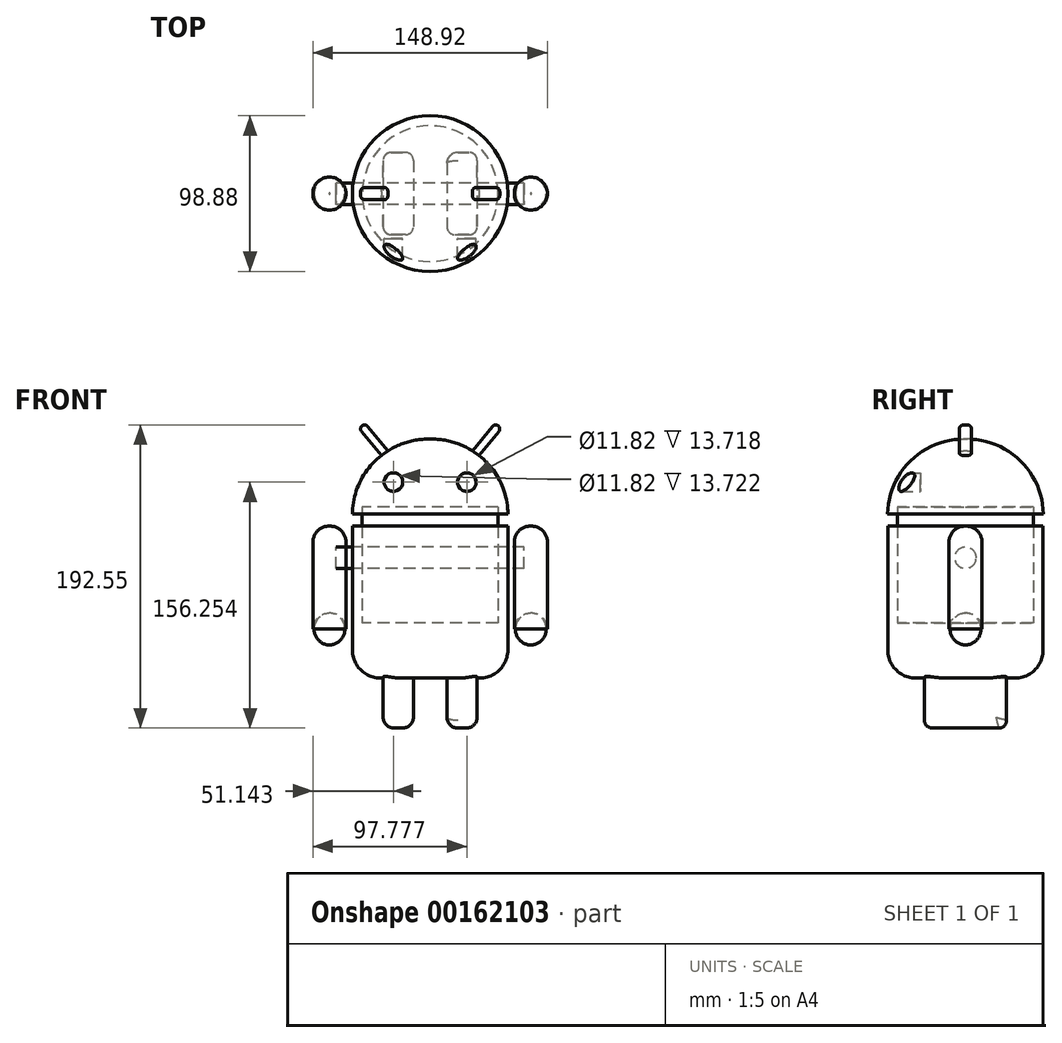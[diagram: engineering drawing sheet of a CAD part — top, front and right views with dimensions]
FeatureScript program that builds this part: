
annotation { "Feature Type Name" : "Feature", "Feature Type Description" : "" }
export const myFeature = defineFeature(function(context is Context, id is Id, definition is map)
    precondition{}
    {
        {
            var Q0;
            Q0=qCreatedBy(makeId("Top.planeOp"),FACE);
            var sketch = newSketch(context, id + "F0", { "sketchPlane" : qUnion([Q0])});
            skCircle(sketch, "E0", {"center": v(0, 0) * mm, "radius": 49.33 * mm});
            skSolve(sketch);
        }
        {
            var Q0;
            Q0=qSketchRegion(id+"F0",true);
            extrude(context, id + "F1", {"entities" : qUnion([Q0]), "depth" : 61.6 * mm, "hasSecondDirection" : true, "secondDirectionOppositeDirection" : true, "secondDirectionDepth" : 34.92 * mm});
        }
        {
            var Q0;
            Q0=makeQuery(id+"F1.opExtrude","CAP_FACE",FACE,{"disambiguationData":[OSD([sQuery(id+"F0.wireOp",EDGE,"E0")])],"isStart":false});
            var sketch = newSketch(context, id + "F2", { "sketchPlane" : qUnion([Q0])});
            skCircle(sketch, "E1", {"center": v(0, 0) * mm, "radius": 49.44 * mm});
            skSolve(sketch);
        }
        {
            var Q0;
            Q0=qSketchRegion(id+"F2",true);
            extrude(context, id + "F3", {"entities" : qUnion([Q0]), "depth" : 55.24 * mm, "hasSecondDirection" : true, "secondDirectionOppositeDirection" : false, "secondDirectionDepth" : 7.62 * mm});
        }
        {
            var Q0;
            Q0=makeQuery(id+"F3.opExtrude","CAP_EDGE",EDGE,{"disambiguationData":[OSD([sQuery(id+"F2.wireOp",EDGE,"E1")])],"isStart":false});
            fillet(context, id + "F4", {"entities" : qUnion([Q0]), "radius" : 48.26 * mm, "tangentPropagation" : true, "allowEdgeOverflow" : false});
        }
        {
            var Q0;
            Q0=makeQuery(id+"F1.opExtrude","CAP_EDGE",EDGE,{"disambiguationData":[OSD([sQuery(id+"F0.wireOp",EDGE,"E0")])],"isStart":true});
            fillet(context, id + "F5", {"entities" : qUnion([Q0]), "radius" : 17.78 * mm, "tangentPropagation" : true, "allowEdgeOverflow" : false});
        }
        {
            var Q0;
            Q0=qCreatedBy(makeId("Top.planeOp"),FACE);
            var sketch = newSketch(context, id + "F6", { "sketchPlane" : qUnion([Q0])});
            skCircle(sketch, "E2", {"center": v(-63.94, 0) * mm, "radius": 10.52 * mm});
            skCircle(sketch, "E3.MirrorC", {"center": v(63.94, 0) * mm, "radius": 10.52 * mm});
            skSolve(sketch);
        }
        {
            var Q0;
            Q0=qSketchRegion(id+"F6",true);
            extrude(context, id + "F7", {"entities" : qUnion([Q0]), "depth" : 61.6 * mm, "hasSecondDirection" : true, "secondDirectionOppositeDirection" : true, "secondDirectionDepth" : 13.97 * mm});
        }
        {
            var Q0;
            Q0=makeQuery(id+"F7.opExtrude","CAP_EDGE",EDGE,{"disambiguationData":[OSD([sQuery(id+"F6.wireOp",EDGE,"E2")])],"isStart":false});
            var Q1;
            Q1=makeQuery(id+"F7.opExtrude","CAP_EDGE",EDGE,{"disambiguationData":[OSD([sQuery(id+"F6.wireOp",EDGE,"E2")])],"isStart":true});
            var Q2;
            Q2=makeQuery(id+"F7.opExtrude","CAP_EDGE",EDGE,{"disambiguationData":[OSD([sQuery(id+"F6.wireOp",EDGE,"E3.MirrorC")])],"isStart":false});
            var Q3;
            Q3=makeQuery(id+"F7.opExtrude","CAP_EDGE",EDGE,{"disambiguationData":[OSD([sQuery(id+"F6.wireOp",EDGE,"E3.MirrorC")])],"isStart":true});
            fillet(context, id + "F8", {"entities" : qUnion([Q0, Q1, Q2, Q3]), "radius" : 10.16 * mm, "tangentPropagation" : true, "allowEdgeOverflow" : false});
        }
        {
            var Q0;
            Q0=qCreatedBy(makeId("Right.planeOp"),FACE);
            var sketch = newSketch(context, id + "F9", { "sketchPlane" : qUnion([Q0])});
            skCircle(sketch, "E4", {"center": v(0, 41.46) * mm, "radius": 6.83 * mm});
            skSolve(sketch);
        }
        {
            var Q0;
            Q0=qSketchRegion(id+"F9",true);
            extrude(context, id + "F10", {"entities" : qUnion([Q0]), "endBound" : BoundingType.SYMMETRIC, "depth" : 119.38 * mm});
        }
        {
            var Q0;
            Q0=qCreatedBy(makeId("Top.planeOp"),FACE);
            var sketch = newSketch(context, id + "F11", { "sketchPlane" : qUnion([Q0])});
            skLineSegment(sketch, "E5.bottom", {"start": v(-10.67, 26.14) * mm, "end": v(-29.84, 26.14) * mm});
            skLineSegment(sketch, "E5.top", {"start": v(-10.67, -26.14) * mm, "end": v(-29.84, -26.14) * mm});
            skLineSegment(sketch, "E5.left", {"start": v(-10.67, 26.14) * mm, "end": v(-10.67, -26.14) * mm});
            skLineSegment(sketch, "E5.right", {"start": v(-29.84, 26.14) * mm, "end": v(-29.84, -26.14) * mm});
            skPoint(sketch, "E5.middle", {"position": v(-20.26, 0) * mm});
            skLineSegment(sketch, "E6.MirrorCS", {"start": v(10.67, 26.14) * mm, "end": v(10.67, -26.14) * mm});
            skLineSegment(sketch, "E7.MirrorCS", {"start": v(10.67, -26.14) * mm, "end": v(29.84, -26.14) * mm});
            skLineSegment(sketch, "E8.MirrorCS", {"start": v(29.84, 26.14) * mm, "end": v(29.84, -26.14) * mm});
            skLineSegment(sketch, "E9.MirrorCS", {"start": v(10.67, 26.14) * mm, "end": v(29.84, 26.14) * mm});
            skSolve(sketch);
        }
        {
            var Q0;
            Q0=qSketchRegion(id+"F11",true);
            extrude(context, id + "F12", {"entities" : qUnion([Q0]), "operationType" : NewBodyOperationType.ADD, "oppositeDirection" : true, "depth" : 66.67 * mm});
        }
        {
            var Q0;
            Q0=makeQuery(id+"F12.opExtrude","SWEPT_EDGE",EDGE,{"disambiguationData":[OSD([sQuery(id+"F11.wireOp",EDGE,"E5.top"),sQuery(id+"F11.wireOp",EDGE,"E5.right")])]});
            var Q1;
            Q1=makeQuery(id+"F12.opExtrude","CAP_EDGE",EDGE,{"disambiguationData":[OSD([sQuery(id+"F11.wireOp",EDGE,"E5.top")])],"isStart":false});
            var Q2;
            Q2=makeQuery(id+"F12.opExtrude","SWEPT_EDGE",EDGE,{"disambiguationData":[OSD([sQuery(id+"F11.wireOp",EDGE,"E5.top"),sQuery(id+"F11.wireOp",EDGE,"E5.left")])]});
            var Q3;
            Q3=makeQuery(id+"F12.opExtrude","SWEPT_EDGE",EDGE,{"disambiguationData":[OSD([sQuery(id+"F11.wireOp",EDGE,"E6.MirrorCS"),sQuery(id+"F11.wireOp",EDGE,"E7.MirrorCS")])]});
            var Q4;
            Q4=makeQuery(id+"F12.opExtrude","SWEPT_EDGE",EDGE,{"disambiguationData":[OSD([sQuery(id+"F11.wireOp",EDGE,"E7.MirrorCS"),sQuery(id+"F11.wireOp",EDGE,"E8.MirrorCS")])]});
            var Q5;
            Q5=makeQuery(id+"F12.opExtrude","CAP_EDGE",EDGE,{"disambiguationData":[OSD([sQuery(id+"F11.wireOp",EDGE,"E7.MirrorCS")])],"isStart":false});
            var Q6;
            Q6=makeQuery(id+"F12.opExtrude","SWEPT_EDGE",EDGE,{"disambiguationData":[OSD([sQuery(id+"F11.wireOp",EDGE,"E8.MirrorCS"),sQuery(id+"F11.wireOp",EDGE,"E9.MirrorCS")])]});
            var Q7;
            Q7=makeQuery(id+"F12.opExtrude","CAP_EDGE",EDGE,{"disambiguationData":[OSD([sQuery(id+"F11.wireOp",EDGE,"E9.MirrorCS")])],"isStart":false});
            var Q8;
            Q8=makeQuery(id+"F12.opExtrude","SWEPT_EDGE",EDGE,{"disambiguationData":[OSD([sQuery(id+"F11.wireOp",EDGE,"E5.bottom"),sQuery(id+"F11.wireOp",EDGE,"E5.right")])]});
            var Q9;
            Q9=makeQuery(id+"F12.opExtrude","SWEPT_EDGE",EDGE,{"disambiguationData":[OSD([sQuery(id+"F11.wireOp",EDGE,"E5.bottom"),sQuery(id+"F11.wireOp",EDGE,"E5.left")])]});
            var Q10;
            Q10=makeQuery(id+"F12.opExtrude","CAP_EDGE",EDGE,{"disambiguationData":[OSD([sQuery(id+"F11.wireOp",EDGE,"E5.bottom")])],"isStart":false});
            fillet(context, id + "F13", {"entities" : qUnion([Q0, Q1, Q2, Q3, Q4, Q5, Q6, Q7, Q8, Q9, Q10]), "radius" : 5.08 * mm, "tangentPropagation" : true, "allowEdgeOverflow" : false});
        }
        {
            var Q0;
            Q0=makeQuery(id+"F12.opExtrude","CAP_EDGE",EDGE,{"disambiguationData":[OSD([sQuery(id+"F11.wireOp",EDGE,"E5.right")])],"isStart":false});
            var Q1;
            Q1=makeQuery(id+"F12.opExtrude","CAP_EDGE",EDGE,{"disambiguationData":[OSD([sQuery(id+"F11.wireOp",EDGE,"E5.left")])],"isStart":false});
            var Q2;
            Q2=makeQuery(id+"F12.opExtrude","CAP_EDGE",EDGE,{"disambiguationData":[OSD([sQuery(id+"F11.wireOp",EDGE,"E6.MirrorCS")])],"isStart":false});
            var Q3;
            Q3=makeQuery(id+"F12.opExtrude","CAP_EDGE",EDGE,{"disambiguationData":[OSD([sQuery(id+"F11.wireOp",EDGE,"E8.MirrorCS")])],"isStart":false});
            fillet(context, id + "F14", {"entities" : qUnion([Q0, Q1, Q2, Q3]), "radius" : 6.86 * mm, "tangentPropagation" : true, "allowEdgeOverflow" : false});
        }
        {
            var Q0;
            Q0=qCreatedBy(makeId("Front.planeOp"),FACE);
            var sketch = newSketch(context, id + "F15", { "sketchPlane" : qUnion([Q0])});
            skCircle(sketch, "E10", {"center": v(-23.32, 89.57) * mm, "radius": 5.91 * mm});
            skCircle(sketch, "E11.MirrorC", {"center": v(23.32, 89.57) * mm, "radius": 5.91 * mm});
            skSolve(sketch);
        }
        {
            var Q0;
            Q0=qSketchRegion(id+"F15",true);
            extrude(context, id + "F16", {"entities" : qUnion([Q0]), "operationType" : NewBodyOperationType.REMOVE, "depth" : 61.6 * mm, "hasSecondDirection" : true, "secondDirectionOppositeDirection" : false, "secondDirectionDepth" : 28.57 * mm});
        }
        {
            var Q0;
            Q0=qCreatedBy(makeId("Front.planeOp"),FACE);
            var sketch = newSketch(context, id + "F17", { "sketchPlane" : qUnion([Q0])});
            skLineSegment(sketch, "E12", {"start": v(-25.65, 104.03) * mm, "end": v(-41.66, 123.33) * mm});
            skArc(sketch, "E13.0.startCap", {"start": v(-23.7, 105.65) * mm, "mid": v(-24.03, 102.07) * mm, "end": v(-27.6, 102.4) * mm});
            skArc(sketch, "E13.0.endCap", {"start": v(-43.62, 121.71) * mm, "mid": v(-43.29, 125.29) * mm, "end": v(-39.7, 124.96) * mm});
            skLineSegment(sketch, "E13.0.left", {"start": v(-27.6, 102.4) * mm, "end": v(-43.62, 121.71) * mm});
            skLineSegment(sketch, "E13.0.right", {"start": v(-23.7, 105.65) * mm, "end": v(-39.7, 124.96) * mm});
            skLineSegment(sketch, "E14.MirrorCS", {"start": v(23.7, 105.65) * mm, "end": v(39.7, 124.96) * mm});
            skArc(sketch, "E15.MirrorCS", {"start": v(43.62, 121.71) * mm, "mid": v(43.29, 125.29) * mm, "end": v(39.7, 124.96) * mm});
            skLineSegment(sketch, "E16.MirrorCS", {"start": v(27.6, 102.4) * mm, "end": v(43.62, 121.71) * mm});
            skArc(sketch, "E17.MirrorCS", {"start": v(23.7, 105.65) * mm, "mid": v(24.03, 102.07) * mm, "end": v(27.6, 102.4) * mm});
            skSolve(sketch);
        }
        {
            var Q0;
            Q0=qSketchRegion(id+"F17",true);
            extrude(context, id + "F18", {"entities" : qUnion([Q0]), "operationType" : NewBodyOperationType.ADD, "endBound" : BoundingType.SYMMETRIC, "depth" : 7.62 * mm});
        }
        {
            var Q0;
            Q0=makeQuery(id+"F18.opExtrude","CAP_EDGE",EDGE,{"disambiguationData":[OSD([sQuery(id+"F17.wireOp",EDGE,"E13.0.right")])],"isStart":false});
            var Q1;
            Q1=makeQuery(id+"F18.opExtrude","CAP_EDGE",EDGE,{"disambiguationData":[OSD([sQuery(id+"F17.wireOp",EDGE,"E13.0.endCap")])],"isStart":false});
            var Q2;
            Q2=makeQuery(id+"F18.opExtrude","CAP_EDGE",EDGE,{"disambiguationData":[OSD([sQuery(id+"F17.wireOp",EDGE,"E13.0.left")])],"isStart":false});
            var Q3;
            Q3=makeQuery(id+"F18.opExtrude","CAP_EDGE",EDGE,{"disambiguationData":[OSD([sQuery(id+"F17.wireOp",EDGE,"E14.MirrorCS")])],"isStart":false});
            var Q4;
            Q4=makeQuery(id+"F18.opExtrude","CAP_EDGE",EDGE,{"disambiguationData":[OSD([sQuery(id+"F17.wireOp",EDGE,"E15.MirrorCS")])],"isStart":false});
            var Q5;
            Q5=makeQuery(id+"F18.opExtrude","CAP_EDGE",EDGE,{"disambiguationData":[OSD([sQuery(id+"F17.wireOp",EDGE,"E16.MirrorCS")])],"isStart":false});
            var Q6;
            Q6=makeQuery(id+"F18.opExtrude","CAP_EDGE",EDGE,{"disambiguationData":[OSD([sQuery(id+"F17.wireOp",EDGE,"E13.0.left")])],"isStart":true});
            var Q7;
            Q7=makeQuery(id+"F18.opExtrude","CAP_EDGE",EDGE,{"disambiguationData":[OSD([sQuery(id+"F17.wireOp",EDGE,"E13.0.endCap")])],"isStart":true});
            var Q8;
            Q8=makeQuery(id+"F18.opExtrude","CAP_EDGE",EDGE,{"disambiguationData":[OSD([sQuery(id+"F17.wireOp",EDGE,"E13.0.right")])],"isStart":true});
            var Q9;
            Q9=makeQuery(id+"F18.opExtrude","CAP_EDGE",EDGE,{"disambiguationData":[OSD([sQuery(id+"F17.wireOp",EDGE,"E14.MirrorCS")])],"isStart":true});
            var Q10;
            Q10=makeQuery(id+"F18.opExtrude","CAP_EDGE",EDGE,{"disambiguationData":[OSD([sQuery(id+"F17.wireOp",EDGE,"E15.MirrorCS")])],"isStart":true});
            fillet(context, id + "F19", {"entities" : qUnion([Q0, Q1, Q2, Q3, Q4, Q5, Q6, Q7, Q8, Q9, Q10]), "radius" : 2.54 * mm, "tangentPropagation" : true, "allowEdgeOverflow" : false});
        }
        {
            var Q0;
            Q0=qCreatedBy(makeId("Top.planeOp"),FACE);
            var sketch = newSketch(context, id + "F20", { "sketchPlane" : qUnion([Q0])});
            skCircle(sketch, "E18", {"center": v(0, 0) * mm, "radius": 43.1 * mm});
            skSolve(sketch);
        }
        {
            var Q0;
            Q0 = qSketchRegion(id + "F20", true);
            extrude(context, id + "F21", {"entities" : qUnion([Q0]), "depth" : 73.66 * mm});
        }
    });
